# Revit family: 4LBS3838FB5T,FB2T,FB5B,FB2B
name_source: partatom
category: Plumbing Fixtures
revit_build: Autodesk Revit LT 2017 (Build: 20161205_1400(x64)
units: mm (PartAtom-declared; Revit-internal decimal feet)

## family parameters
Always vertical = Yes
Cut with Voids When Loaded = No
OmniClass Number = 23.45.05.14.17
OmniClass Title = Showers
Part Type = Normal
Room Calculation Point = No
Round Connector Dimension = Use Diameter
Shared = No
Work Plane-Based = No

## types (4) — shared parameters
Assembly Code = D2010710
Keynote = 22 40 00.B3
Manufacturer = Best Bath Systems, Inc.
Type Comments = Barrier Free
URL = http://www.bestbath.com
Unit Depth = 38 1/4"
Unit Width = 38 1/2"

## per-type parameters (varying)
| type | Description | Threshold Height | Unit Height |
| 4LBS3838FB5B | 4 x 8 Subway Tile, Beveled Threshold | 5/8" | 80 1/8" |
| 4LBS3838FB2B | 4 x 8 Subway Tile, Beveled Threshold | 2" | 81 1/2" |
| 4LBS3838FB5T | 4 x 8 Subway Tile, Traditional Bull Nose Threshold | 5/8" | 80 1/8" |
| 4LBS3838FB2T | 4 x 8 Tile, Traditional Bull Nose Threshold | 2" | 81 1/2" |

note: column(s) folded — value = type name in every type: Model

## geometry (parser evidence)
native form markers: Blend x4, Sweep x1
no freeform markers — native parametric forms only
